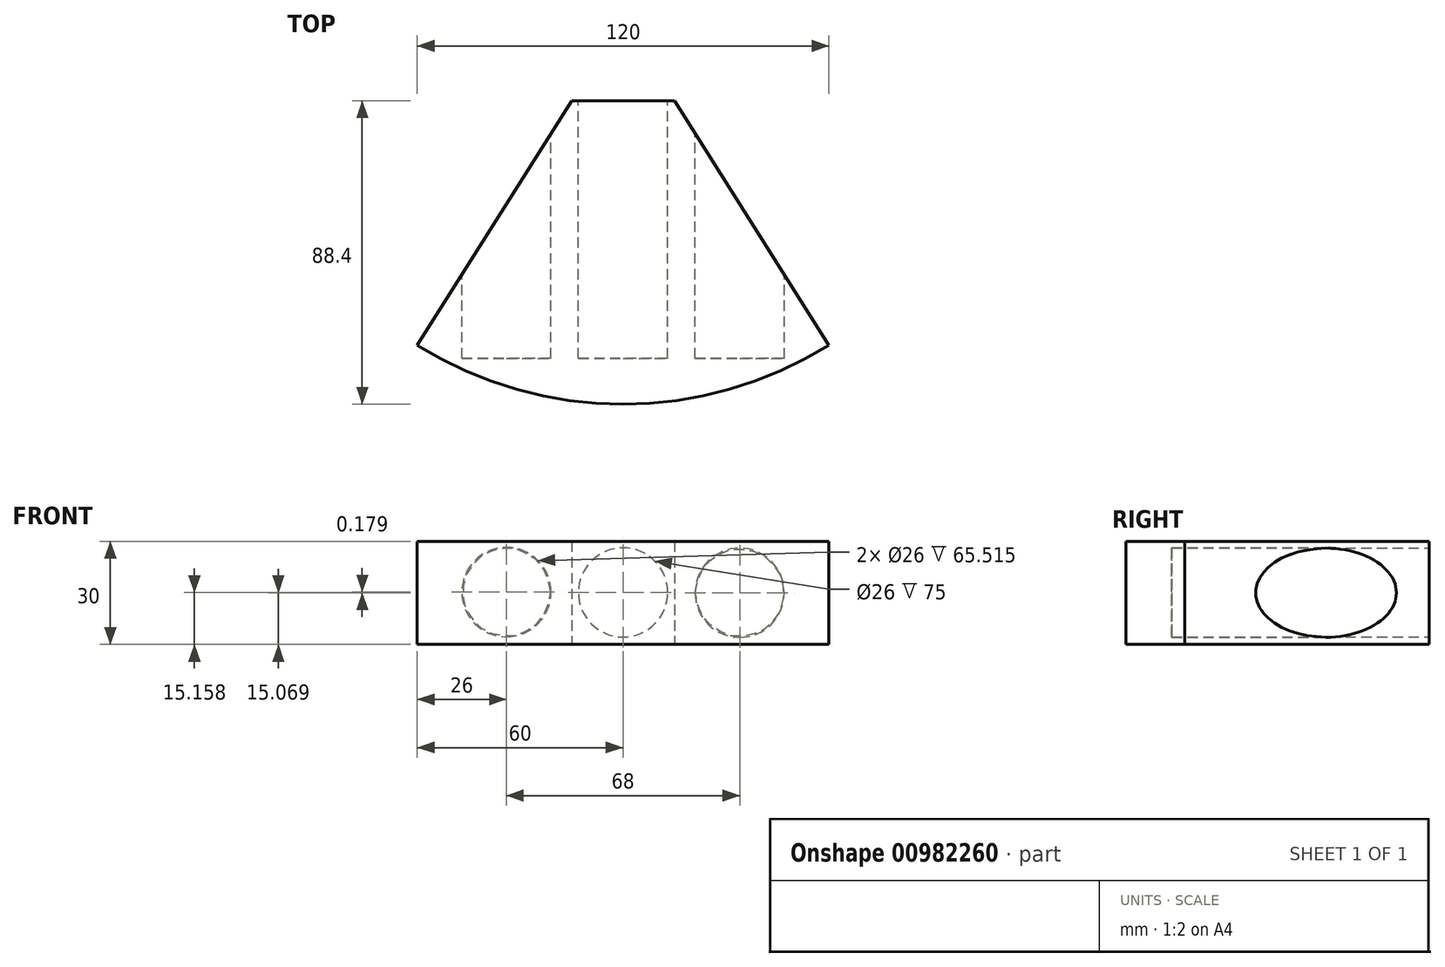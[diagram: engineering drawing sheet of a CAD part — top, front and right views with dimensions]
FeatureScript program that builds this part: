
annotation { "Feature Type Name" : "Feature", "Feature Type Description" : "" }
export const myFeature = defineFeature(function(context is Context, id is Id, definition is map)
    precondition{}
    {
        {
            var Q0;
            Q0=qCreatedBy(makeId("Top.planeOp"),FACE);
            var sketch = newSketch(context, id + "F0", { "sketchPlane" : qUnion([Q0])});
            skLineSegment(sketch, "E0", {"start": v(0, -71.21) * mm, "end": v(0, 0) * mm});
            skLineSegment(sketch, "E1", {"start": v(-15, 0) * mm, "end": v(15, 0) * mm});
            skArc(sketch, "E2", {"start": v(-60, -71.21) * mm, "mid": v(0, -88.4) * mm, "end": v(60, -71.21) * mm});
            skLineSegment(sketch, "E3", {"start": v(-15, 0) * mm, "end": v(-60, -71.21) * mm});
            skLineSegment(sketch, "E4", {"start": v(15, 0) * mm, "end": v(60, -71.21) * mm});
            skLineSegment(sketch, "E5", {"start": v(0, -7.32) * mm, "end": v(0, 19.36) * mm, "construction": true});
            skLineSegment(sketch, "E6", {"start": v(45.5, 0) * mm, "end": v(-51.8, 0) * mm, "construction": true});
            skSolve(sketch);
        }
        {
            var Q0;
            Q0=makeQuery(id+"F0.imprint","IMPRINT",FACE,{"disambiguationData":[TD([[makeQuery(id+"F0.imprint","IMPRINT",EDGE,{"derivedFrom":sQuery(id+"F0.wireOp",EDGE,"E2")}),1.0]])]});
            extrude(context, id + "F1", {"entities" : qUnion([Q0]), "depth" : 30 * mm, "offsetDistance" : 25 * mm});
        }
        {
            var Q0;
            Q0=sQuery(id+"F0.wireOp",EDGE,"E2");
            extrude(context, id + "F2", {"bodyType" : ToolBodyType.SURFACE, "surfaceEntities" : qUnion([Q0]), "endBound" : BoundingType.SYMMETRIC, "depth" : 60 * mm, "offsetDistance" : 25 * mm});
        }
        {
            var Q0;
            Q0=qCreatedBy(makeId("Front.planeOp"),FACE);
            var sketch = newSketch(context, id + "F3", { "sketchPlane" : qUnion([Q0])});
            skCircle(sketch, "E7", {"center": v(0, 15.16) * mm, "radius": 11 * mm});
            skCircle(sketch, "E8", {"center": v(-34, 15.25) * mm, "radius": 11 * mm});
            skCircle(sketch, "E9", {"center": v(34, 15.07) * mm, "radius": 11 * mm});
            skLineSegment(sketch, "E10", {"start": v(-62.57, 15.32) * mm, "end": v(92.7, 14.91) * mm, "construction": true});
            skCircle(sketch, "E11.0", {"center": v(-34, 15.25) * mm, "radius": 13 * mm});
            skCircle(sketch, "E12.0", {"center": v(0, 15.16) * mm, "radius": 13 * mm});
            skCircle(sketch, "E13.0", {"center": v(34, 15.07) * mm, "radius": 13 * mm});
            skLineSegment(sketch, "E14", {"start": v(0, -43.93) * mm, "end": v(0.26, 54.82) * mm, "construction": true});
            skSolve(sketch);
        }
        {
            var Q0;
            Q0 = qSketchRegion(id + "F3", true);
            var Q1;
            Q1=makeQuery(id+"F3.imprint","IMPRINT",FACE,{"disambiguationData":[TD([[makeQuery(id+"F3.imprint","IMPRINT",EDGE,{"derivedFrom":sQuery(id+"F3.wireOp",EDGE,"E7")}),1.0]])]});
            var Q2;
            Q2=makeQuery(id+"F3.imprint","IMPRINT",FACE,{"disambiguationData":[TD([[makeQuery(id+"F3.imprint","IMPRINT",EDGE,{"derivedFrom":sQuery(id+"F3.wireOp",EDGE,"E9")}),1.0]])]});
            var Q3;
            Q3=makeQuery(id+"F3.imprint","IMPRINT",FACE,{"disambiguationData":[TD([[makeQuery(id+"F3.imprint","IMPRINT",EDGE,{"derivedFrom":sQuery(id+"F3.wireOp",EDGE,"E8")}),1.0]])]});
            extrude(context, id + "F4", {"entities" : qUnion([Q0, Q1, Q2, Q3]), "operationType" : NewBodyOperationType.REMOVE, "depth" : 75 * mm, "offsetDistance" : 25 * mm});
        }
    });
